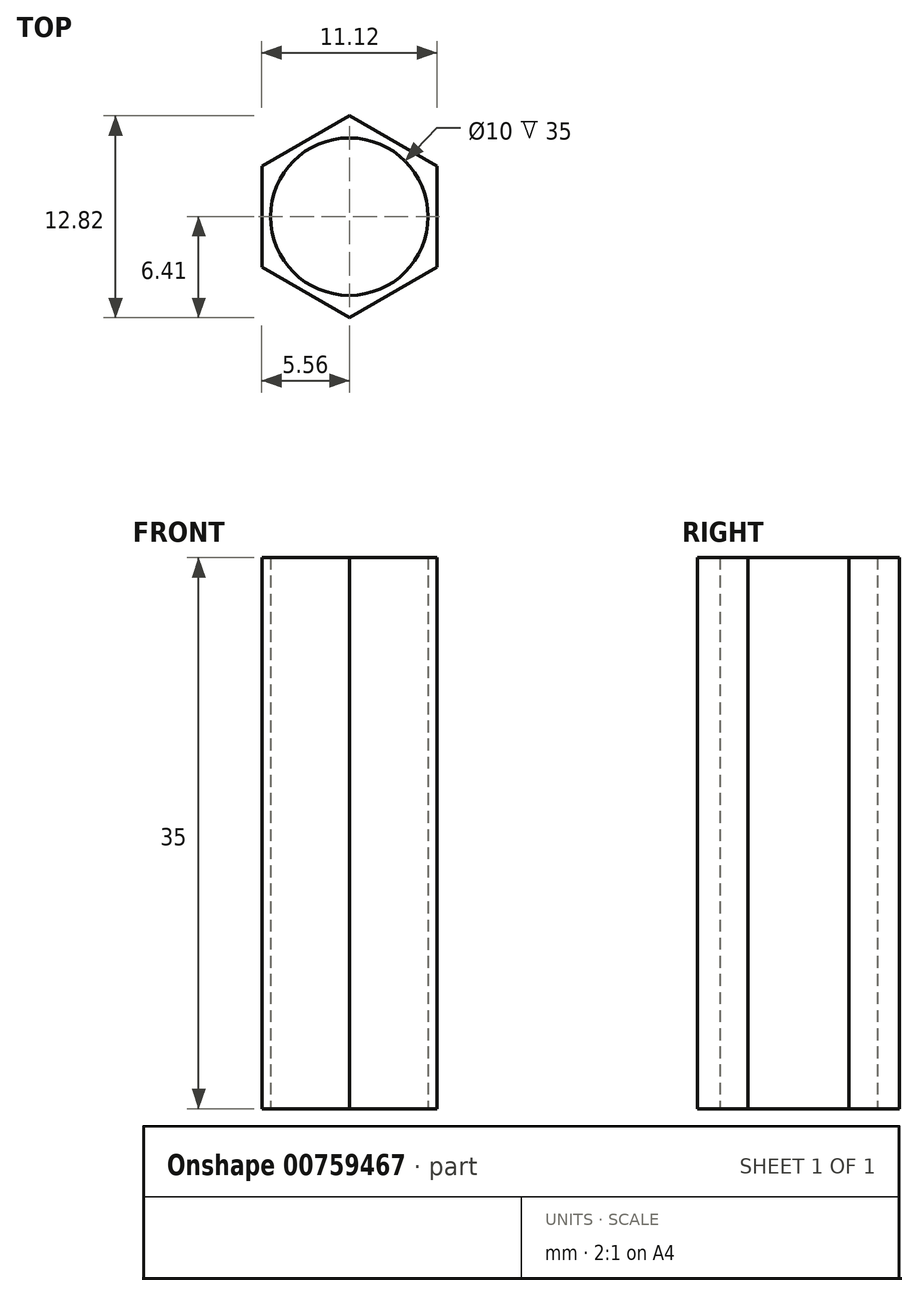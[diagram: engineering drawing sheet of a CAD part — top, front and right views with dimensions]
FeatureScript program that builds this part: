
annotation { "Feature Type Name" : "Feature", "Feature Type Description" : "" }
export const myFeature = defineFeature(function(context is Context, id is Id, definition is map)
    precondition{}
    {
        {
            var Q0;
            Q0=qCreatedBy(makeId("Top.planeOp"),FACE);
            var sketch = newSketch(context, id + "F0", { "sketchPlane" : qUnion([Q0])});
            skCircle(sketch, "E0.cCircle", {"center": v(0, 0) * mm, "radius": 5.55 * mm, "construction": true});
            skLineSegment(sketch, "E0.0", {"start": v(5.55, 3.2) * mm, "end": v(5.55, -3.2) * mm});
            skLineSegment(sketch, "E0.1", {"start": v(5.55, -3.2) * mm, "end": v(0, -6.41) * mm});
            skLineSegment(sketch, "E0.2", {"start": v(0, -6.41) * mm, "end": v(-5.55, -3.2) * mm});
            skLineSegment(sketch, "E0.3", {"start": v(-5.55, -3.2) * mm, "end": v(-5.56, 3.2) * mm});
            skLineSegment(sketch, "E0.4", {"start": v(-5.55, 3.2) * mm, "end": v(0, 6.41) * mm});
            skLineSegment(sketch, "E0.5", {"start": v(0, 6.41) * mm, "end": v(5.55, 3.2) * mm});
            skPoint(sketch, "E0.0.midPoint", {"position": v(5.55, 0) * mm});
            skCircle(sketch, "E1", {"center": v(0, 0) * mm, "radius": 5 * mm});
            skSolve(sketch);
        }
        {
            var Q0;
            Q0 = qSketchRegion(id + "F0", true);
            extrude(context, id + "F1", {"entities" : qUnion([Q0]), "depth" : 35 * mm, "offsetDistance" : 25 * mm});
        }
    });
